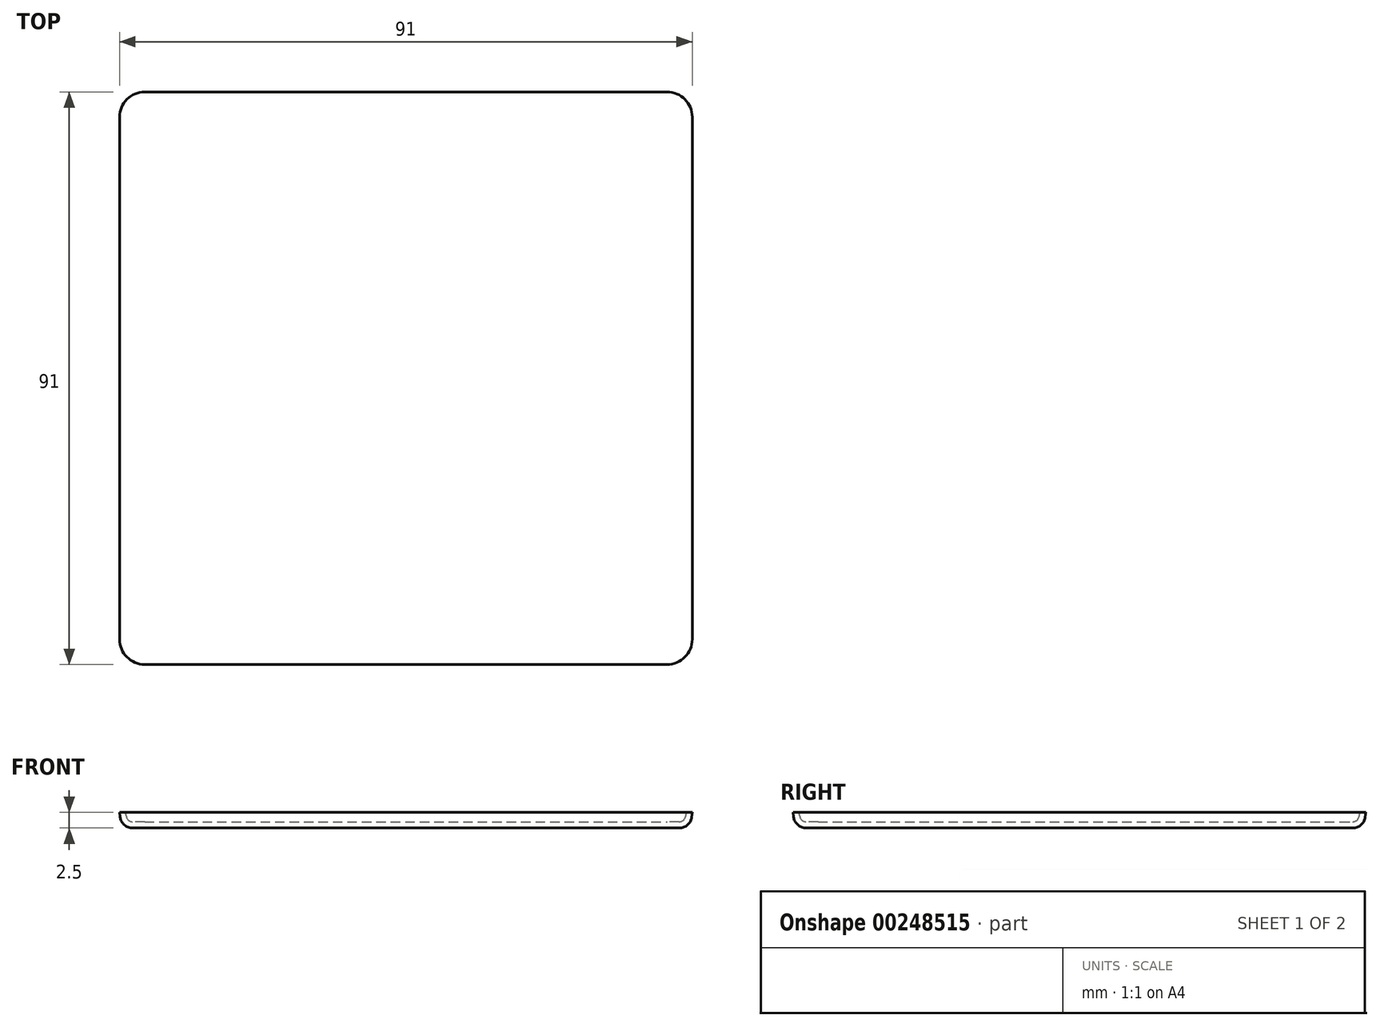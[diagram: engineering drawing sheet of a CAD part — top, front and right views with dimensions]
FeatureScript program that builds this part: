
annotation { "Feature Type Name" : "Feature", "Feature Type Description" : "" }
export const myFeature = defineFeature(function(context is Context, id is Id, definition is map)
    precondition{}
    {
        {
            var Q0;
            Q0=qCreatedBy(makeId("Top.planeOp"),FACE);
            var sketch = newSketch(context, id + "F0", { "sketchPlane" : qUnion([Q0])});
            skLineSegment(sketch, "E0.bottom", {"start": v(45.5, -45.5) * mm, "end": v(-45.5, -45.5) * mm});
            skLineSegment(sketch, "E0.top", {"start": v(45.5, 45.5) * mm, "end": v(-45.5, 45.5) * mm});
            skLineSegment(sketch, "E0.left", {"start": v(45.5, -45.5) * mm, "end": v(45.5, 45.5) * mm});
            skLineSegment(sketch, "E0.right", {"start": v(-45.5, -45.5) * mm, "end": v(-45.5, 45.5) * mm});
            skPoint(sketch, "E0.middle", {"position": v(0, 0) * mm});
            skSolve(sketch);
        }
        {
            var Q0;
            Q0=makeQuery(id+"F0.imprint","IMPRINT",FACE,{"disambiguationData":[TD([[makeQuery(id+"F0.imprint","IMPRINT",EDGE,{"derivedFrom":sQuery(id+"F0.wireOp",EDGE,"E0.bottom")}),-1.0]])]});
            extrude(context, id + "F1", {"entities" : qUnion([Q0]), "depth" : 2.5 * mm});
        }
        {
            var Q0;
            Q0=makeQuery(id+"F1.opExtrude","SWEPT_EDGE",EDGE,{"disambiguationData":[OSD([sQuery(id+"F0.wireOp",EDGE,"E0.bottom"),sQuery(id+"F0.wireOp",EDGE,"E0.right")])]});
            var Q1;
            Q1=makeQuery(id+"F1.opExtrude","SWEPT_EDGE",EDGE,{"disambiguationData":[OSD([sQuery(id+"F0.wireOp",EDGE,"E0.top"),sQuery(id+"F0.wireOp",EDGE,"E0.right")])]});
            var Q2;
            Q2=makeQuery(id+"F1.opExtrude","SWEPT_EDGE",EDGE,{"disambiguationData":[OSD([sQuery(id+"F0.wireOp",EDGE,"E0.top"),sQuery(id+"F0.wireOp",EDGE,"E0.left")])]});
            var Q3;
            Q3=makeQuery(id+"F1.opExtrude","SWEPT_EDGE",EDGE,{"disambiguationData":[OSD([sQuery(id+"F0.wireOp",EDGE,"E0.bottom"),sQuery(id+"F0.wireOp",EDGE,"E0.left")])]});
            fillet(context, id + "F2", {"entities" : qUnion([Q0, Q1, Q2, Q3]), "radius" : 4 * mm, "tangentPropagation" : true, "allowEdgeOverflow" : false});
        }
        {
            var Q0;
            Q0=makeQuery(id+"F1.opExtrude","CAP_EDGE",EDGE,{"disambiguationData":[OSD([sQuery(id+"F0.wireOp",EDGE,"E0.bottom")])],"isStart":true});
            chamfer(context, id + "F3", {"entities" : qUnion([Q0]), "chamferType" : ChamferType.TWO_OFFSETS, "width1" : 0.3 * mm, "oppositeDirection" : false, "width2" : 2.5 * mm, "tangentPropagation" : true});
        }
        {
            var Q0;
            {var subQ0=sQuery(id+"F0.wireOp",EDGE,"E0.bottom");Q0=makeQuery(id+"F3.opChamfer","BLEND_EDGE",EDGE,{"blendedFrom":[makeQuery(id+"F1.opExtrude","CAP_EDGE",EDGE,{"disambiguationData":[OSD([subQ0])],"isStart":true}),makeQuery(id+"F1.opExtrude","CAP_FACE",FACE,{"disambiguationData":[OSD([subQ0,sQuery(id+"F0.wireOp",EDGE,"E0.top"),sQuery(id+"F0.wireOp",EDGE,"E0.left"),sQuery(id+"F0.wireOp",EDGE,"E0.right")])],"isStart":true})],"blendedInto":[makeQuery(id+"F1.opExtrude","CAP_FACE",FACE,{"disambiguationData":[OSD([subQ0,sQuery(id+"F0.wireOp",EDGE,"E0.top"),sQuery(id+"F0.wireOp",EDGE,"E0.left"),sQuery(id+"F0.wireOp",EDGE,"E0.right")])],"isStart":true})]});}
            fillet(context, id + "F4", {"entities" : qUnion([Q0]), "radius" : 2 * mm, "tangentPropagation" : true, "allowEdgeOverflow" : false});
        }
        {
            var Q0;
            Q0=makeQuery(id+"F1.opExtrude","CAP_FACE",FACE,{"disambiguationData":[OSD([sQuery(id+"F0.wireOp",EDGE,"E0.bottom"),sQuery(id+"F0.wireOp",EDGE,"E0.top"),sQuery(id+"F0.wireOp",EDGE,"E0.left"),sQuery(id+"F0.wireOp",EDGE,"E0.right")])],"isStart":false});
            shell(context, id + "F5", {"entities" : qUnion([Q0]), "thickness" : 1 * mm});
        }
        {
            var Q0;
            {var subQ0=sQuery(id+"F0.wireOp",EDGE,"E0.right");var subQ1=sQuery(id+"F0.wireOp",EDGE,"E0.left");var subQ2=sQuery(id+"F0.wireOp",EDGE,"E0.top");var subQ3=sQuery(id+"F0.wireOp",EDGE,"E0.bottom");Q0=makeQuery(id+"F5.opShell","OFFSET_EDGE",EDGE,{"disambiguationData":[OSD([subQ3,subQ2,subQ1,subQ0]),TDD([makeQuery(id+"F3.opChamfer","BLEND_EDGE",EDGE,{"blendedFrom":[makeQuery(id+"F1.opExtrude","CAP_EDGE",EDGE,{"disambiguationData":[OSD([subQ0])],"isStart":true}),makeQuery(id+"F1.opExtrude","CAP_FACE",FACE,{"disambiguationData":[OSD([subQ3,subQ2,subQ1,subQ0])],"isStart":false})],"blendedInto":[makeQuery(id+"F1.opExtrude","CAP_FACE",FACE,{"disambiguationData":[OSD([subQ3,subQ2,subQ1,subQ0])],"isStart":false})]})])]});}
            fillet(context, id + "F6", {"entities" : qUnion([Q0]), "radius" : 0.5 * mm, "tangentPropagation" : true, "allowEdgeOverflow" : false});
        }
    });
